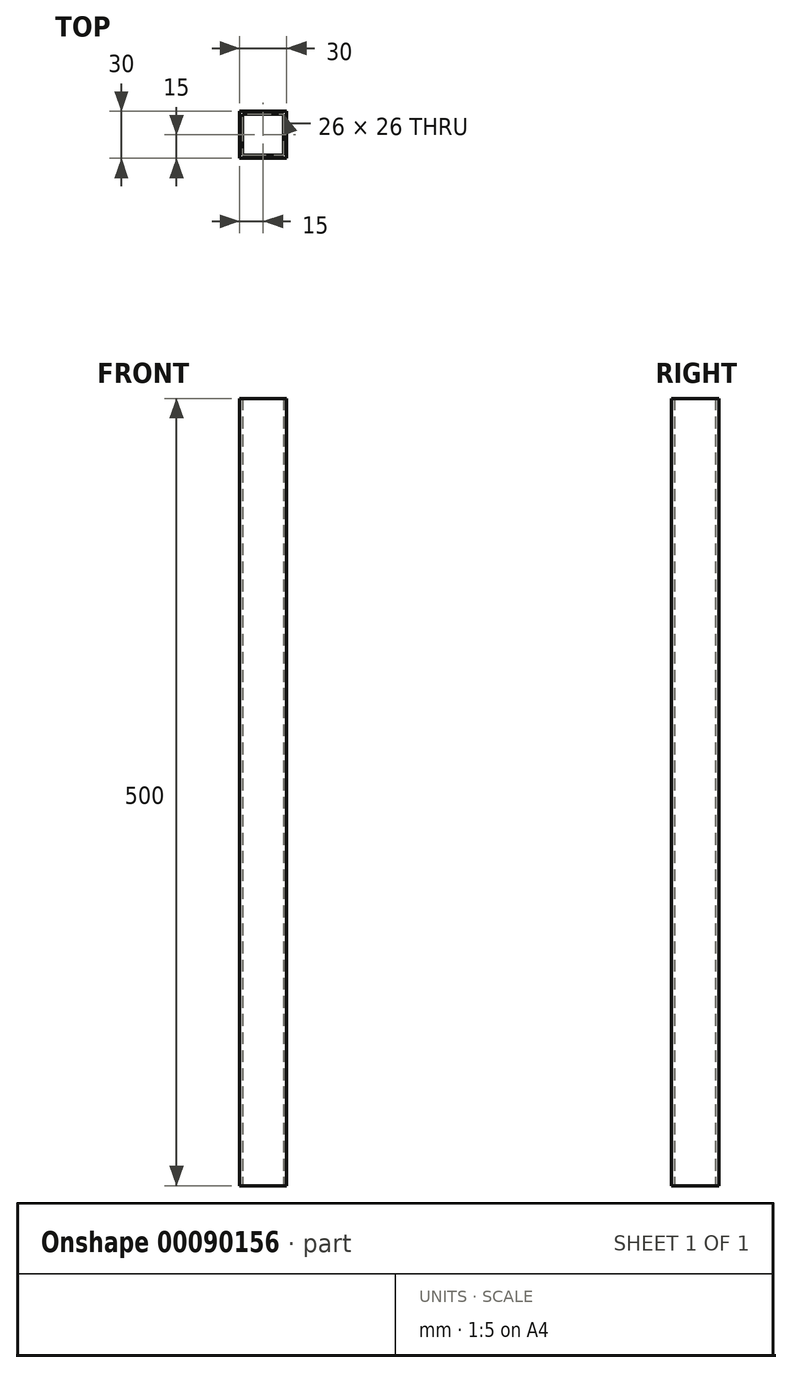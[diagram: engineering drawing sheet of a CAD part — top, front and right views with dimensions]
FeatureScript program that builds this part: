
annotation { "Feature Type Name" : "Feature", "Feature Type Description" : "" }
export const myFeature = defineFeature(function(context is Context, id is Id, definition is map)
    precondition{}
    {
        {
            var Q0;
            Q0=qCreatedBy(makeId("Top.planeOp"),FACE);
            var sketch = newSketch(context, id + "F0", { "sketchPlane" : qUnion([Q0])});
            skPoint(sketch, "E0.middle", {"position": v(0, 0) * mm});
            skLineSegment(sketch, "E1.bottom", {"start": v(15, -15) * mm, "end": v(-15, -15) * mm});
            skLineSegment(sketch, "E1.top", {"start": v(15, 15) * mm, "end": v(-15, 15) * mm});
            skLineSegment(sketch, "E1.left", {"start": v(15, -15) * mm, "end": v(15, 15) * mm});
            skLineSegment(sketch, "E1.right", {"start": v(-15, -15) * mm, "end": v(-15, 15) * mm});
            skLineSegment(sketch, "E2.bottom", {"start": v(13, -13) * mm, "end": v(-13, -13) * mm});
            skLineSegment(sketch, "E2.top", {"start": v(13, 13) * mm, "end": v(-13, 13) * mm});
            skLineSegment(sketch, "E2.left", {"start": v(13, -13) * mm, "end": v(13, 13) * mm});
            skLineSegment(sketch, "E2.right", {"start": v(-13, -13) * mm, "end": v(-13, 13) * mm});
            skSolve(sketch);
        }
        {
            var Q0;
            Q0 = qSketchRegion(id + "F0", true);
            extrude(context, id + "F1", {"entities" : qUnion([Q0]), "depth" : 500 * mm});
        }
    });
